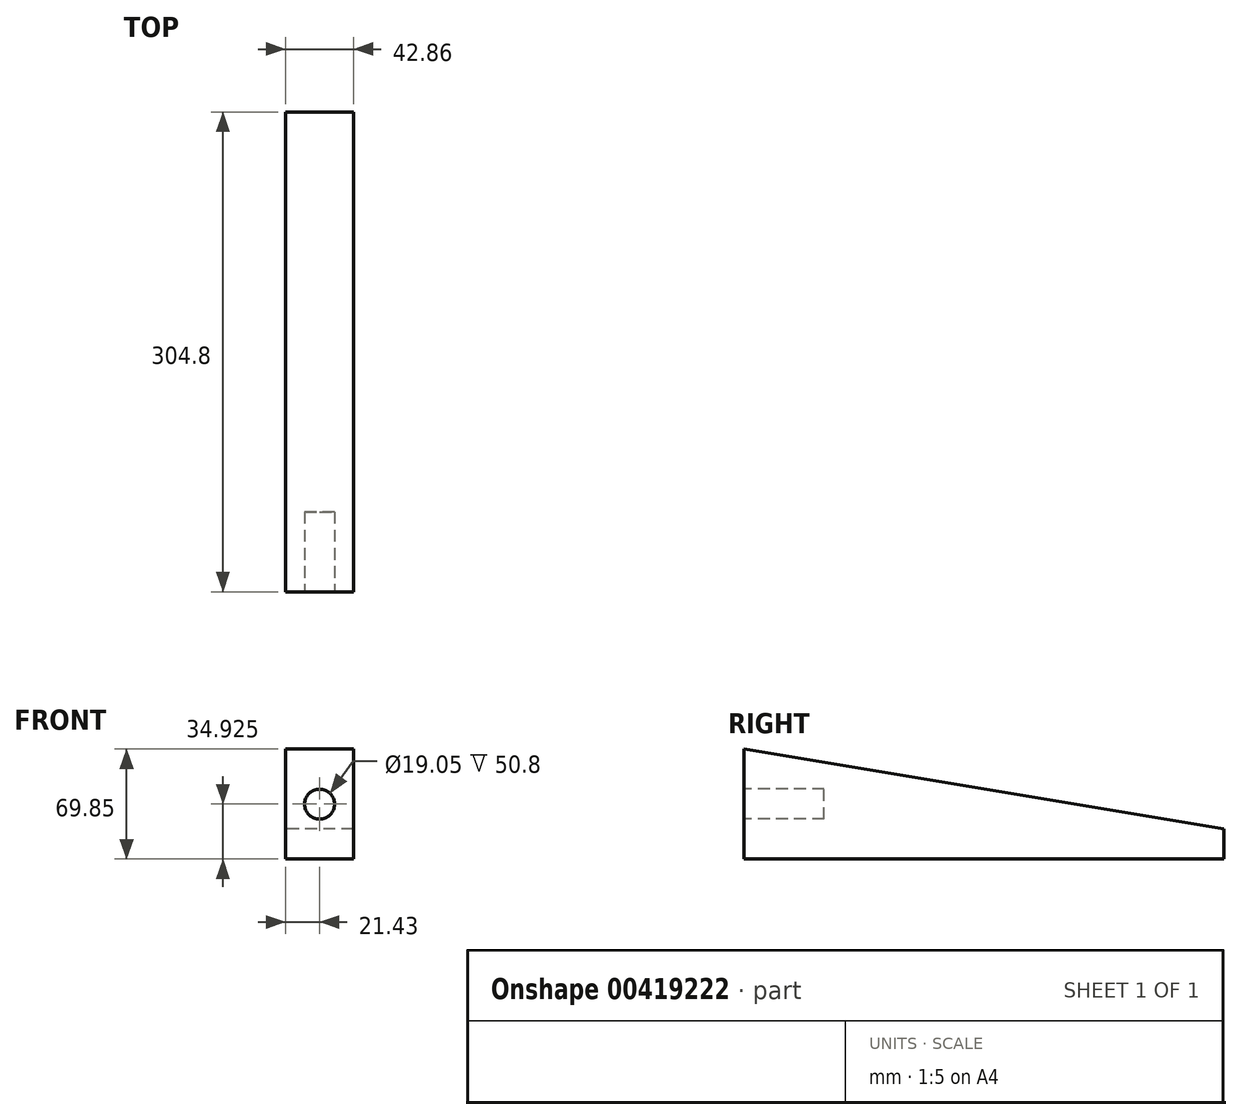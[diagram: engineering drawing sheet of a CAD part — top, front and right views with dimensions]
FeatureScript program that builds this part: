
annotation { "Feature Type Name" : "Feature", "Feature Type Description" : "" }
export const myFeature = defineFeature(function(context is Context, id is Id, definition is map)
    precondition{}
    {
        {
            var Q0;
            Q0=qCreatedBy(makeId("Right.planeOp"),FACE);
            var sketch = newSketch(context, id + "F0", { "sketchPlane" : qUnion([Q0])});
            skLineSegment(sketch, "E0", {"start": v(-152.4, 0) * mm, "end": v(152.4, 0) * mm});
            skLineSegment(sketch, "E1", {"start": v(-152.4, 0) * mm, "end": v(-152.4, 69.85) * mm});
            skLineSegment(sketch, "E2", {"start": v(152.4, 0) * mm, "end": v(152.4, 19.05) * mm});
            skLineSegment(sketch, "E3", {"start": v(152.4, 19.05) * mm, "end": v(-152.4, 69.85) * mm});
            skPoint(sketch, "E4.endSnap0", {"position": v(-152.4, 34.93) * mm});
            skLineSegment(sketch, "E5.0", {"start": v(-95.25, 50.8) * mm, "end": v(-152.4, 50.8) * mm, "construction": true});
            skLineSegment(sketch, "E5.1", {"start": v(-95.25, 50.8) * mm, "end": v(-95.25, 19.05) * mm, "construction": true});
            skLineSegment(sketch, "E5.2", {"start": v(-95.25, 19.05) * mm, "end": v(-152.4, 19.05) * mm, "construction": true});
            skSolve(sketch);
        }
        {
            var Q0;
            Q0=makeQuery(id+"F0.imprint","IMPRINT",FACE,{"disambiguationData":[TD([[makeQuery(id+"F0.imprint","IMPRINT",EDGE,{"derivedFrom":sQuery(id+"F0.wireOp",EDGE,"E0")}),1.0]])]});
            extrude(context, id + "F1", {"entities" : qUnion([Q0]), "depth" : 42.86 * mm, "symmetric" : true});
        }
        {
            var Q0;
            Q0=makeQuery(id+"F1.opExtrude","SWEPT_FACE",FACE,{"disambiguationData":[OSD([sQuery(id+"F0.wireOp",EDGE,"E1")])]});
            var sketch = newSketch(context, id + "F2", { "sketchPlane" : qUnion([Q0])});
            skLineSegment(sketch, "E6", {"start": v(21.43, 34.93) * mm, "end": v(0, 34.93) * mm, "construction": true});
            skCircle(sketch, "E7", {"center": v(0, 34.93) * mm, "radius": 9.53 * mm});
            skSolve(sketch);
        }
        {
            var Q0;
            Q0=makeQuery(id+"F2.imprint","IMPRINT",FACE,{"disambiguationData":[TD([[makeQuery(id+"F2.imprint","IMPRINT",EDGE,{"derivedFrom":sQuery(id+"F2.wireOp",EDGE,"E7")}),1.0]])]});
            var Q1;
            Q1=sQuery(id+"F2.wireOp",EDGE,"E7");
            extrude(context, id + "F3", {"entities" : qUnion([Q0]), "operationType" : NewBodyOperationType.REMOVE, "surfaceEntities" : qUnion([Q1]), "oppositeDirection" : true, "depth" : 50.8 * mm});
        }
    });
